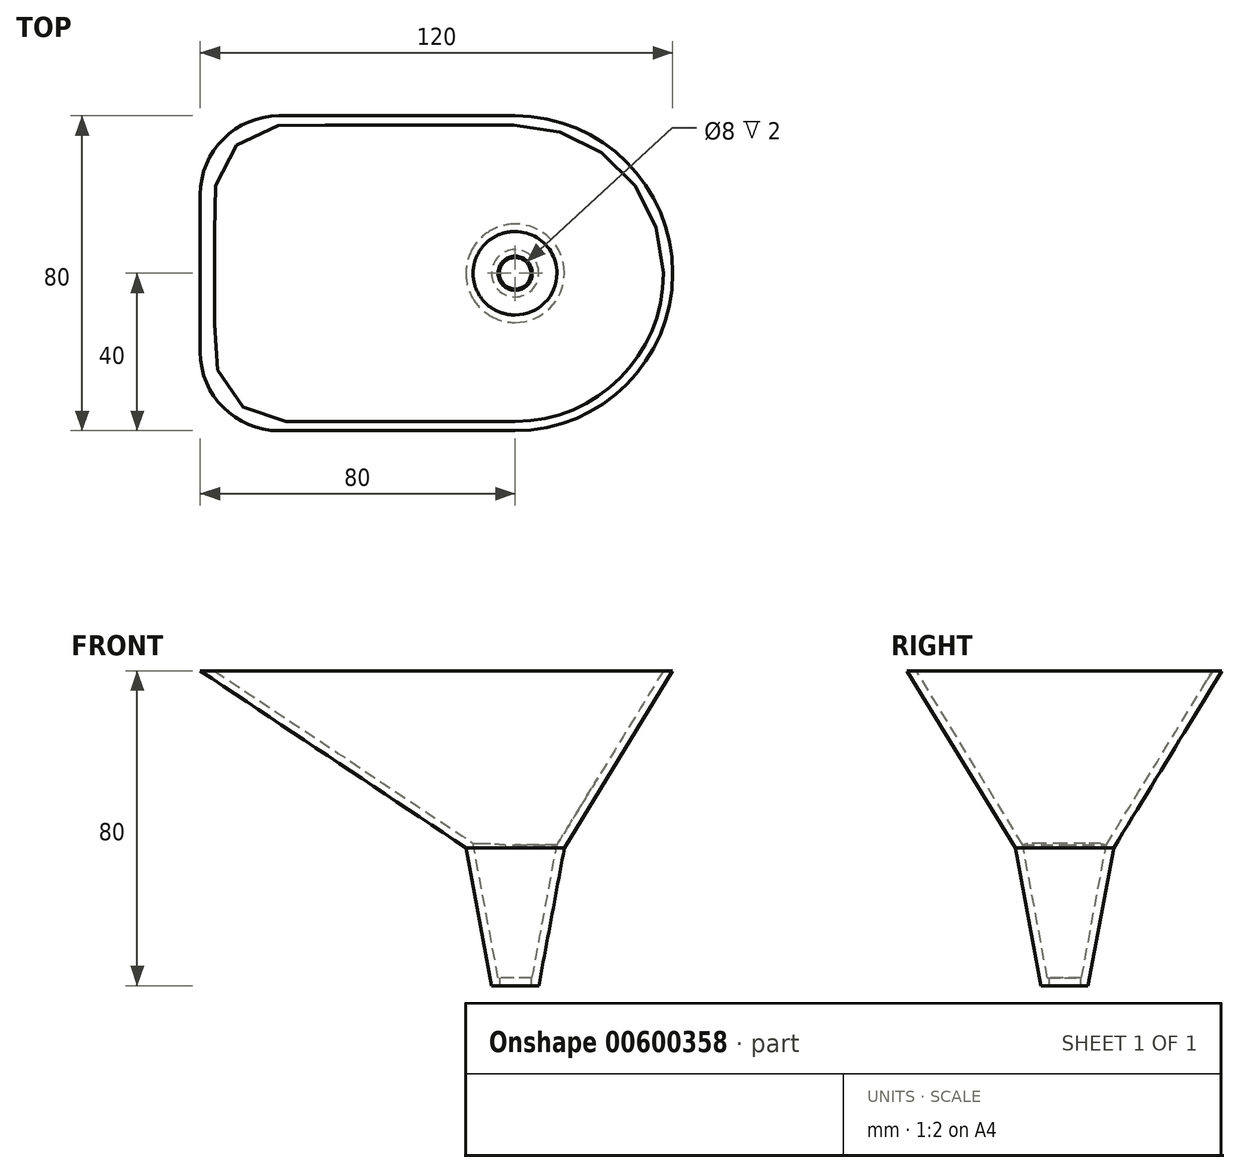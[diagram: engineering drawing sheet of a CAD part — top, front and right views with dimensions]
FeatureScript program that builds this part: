
annotation { "Feature Type Name" : "Feature", "Feature Type Description" : "" }
export const myFeature = defineFeature(function(context is Context, id is Id, definition is map)
    precondition{}
    {
        {
            var Q0;
            Q0=qCreatedBy(makeId("Top.planeOp"),FACE);
            var sketch = newSketch(context, id + "F0", { "sketchPlane" : qUnion([Q0])});
            skCircle(sketch, "E0", {"center": v(0, 0) * mm, "radius": 12.5 * mm});
            skSolve(sketch);
        }
        {
            var Q0;
            Q0=qCreatedBy(makeId("Top.planeOp"),FACE);
            cPlane(context, id + "F1", {"entities" : qUnion([Q0]), "cplaneType" : CPlaneType.OFFSET, "offset" : 35 * mm, "oppositeDirection" : true, "width" : 150 * mm, "height" : 150 * mm});
        }
        {
            var Q0;
            Q0=qCreatedBy(id+"F1.planeOp",FACE);
            var sketch = newSketch(context, id + "F2", { "sketchPlane" : qUnion([Q0])});
            skCircle(sketch, "E1", {"center": v(0, 0) * mm, "radius": 6 * mm});
            skSolve(sketch);
        }
        {
            var Q0;
            Q0=qCreatedBy(makeId("Top.planeOp"),FACE);
            cPlane(context, id + "F3", {"entities" : qUnion([Q0]), "cplaneType" : CPlaneType.OFFSET, "offset" : 45 * mm, "width" : 150 * mm, "height" : 150 * mm});
        }
        {
            var Q0;
            Q0=makeQuery(id+"F2.imprint","IMPRINT",FACE,{"disambiguationData":[TD([[makeQuery(id+"F2.imprint","IMPRINT",EDGE,{"derivedFrom":sQuery(id+"F2.wireOp",EDGE,"E1")}),1.0]])]});
            var Q1;
            Q1=makeQuery(id+"F0.imprint","IMPRINT",FACE,{"disambiguationData":[TD([[makeQuery(id+"F0.imprint","IMPRINT",EDGE,{"derivedFrom":sQuery(id+"F0.wireOp",EDGE,"E0")}),1.0]])]});
            loft(context, id + "F4", {"sheetProfilesArray" : [{ "sheetProfileEntities" : qUnion([Q0]) }, { "sheetProfileEntities" : qUnion([Q1]) }]});
        }
        {
            var Q0;
            Q0=qCreatedBy(id+"F3.planeOp",FACE);
            var sketch = newSketch(context, id + "F5", { "sketchPlane" : qUnion([Q0])});
            skLineSegment(sketch, "E2", {"start": v(0, 40) * mm, "end": v(-60, 40) * mm});
            skLineSegment(sketch, "E3", {"start": v(-80, 20) * mm, "end": v(-80, -20) * mm});
            skLineSegment(sketch, "E4", {"start": v(-60, -40) * mm, "end": v(0, -40) * mm});
            skArc(sketch, "E5", {"start": v(0, 40) * mm, "mid": v(40, 0) * mm, "end": v(0, -40) * mm});
            skPoint(sketch, "E6.visualSharp", {"position": v(-80, 40) * mm});
            skArc(sketch, "E6.filletArc", {"start": v(-60, 40) * mm, "mid": v(-74.14, 34.14) * mm, "end": v(-80, 20) * mm});
            skPoint(sketch, "E7.visualSharp", {"position": v(-80, -40) * mm});
            skArc(sketch, "E7.filletArc", {"start": v(-80, -20) * mm, "mid": v(-74.14, -34.14) * mm, "end": v(-60, -40) * mm});
            skSolve(sketch);
        }
        {
            var Q0;
            Q0=qCreatedBy(makeId("Front.planeOp"),FACE);
            var sketch = newSketch(context, id + "F6", { "sketchPlane" : qUnion([Q0])});
            skLineSegment(sketch, "E8", {"start": v(40, 45) * mm, "end": v(12.5, 0) * mm});
            skLineSegment(sketch, "E9", {"start": v(-80, 45) * mm, "end": v(-12.5, 0) * mm});
            skSolve(sketch);
        }
        {
            var Q0;
            Q0=qCreatedBy(makeId("Right.planeOp"),FACE);
            var sketch = newSketch(context, id + "F7", { "sketchPlane" : qUnion([Q0])});
            skLineSegment(sketch, "E10", {"start": v(-40, 45) * mm, "end": v(-12.5, 0) * mm});
            skLineSegment(sketch, "E11", {"start": v(40, 45) * mm, "end": v(12.5, 0) * mm});
            skSolve(sketch);
        }
        {
            var Q0;
            Q0=makeQuery(id+"F5.imprint","IMPRINT",FACE,{"disambiguationData":[TD([[makeQuery(id+"F5.imprint","IMPRINT",EDGE,{"derivedFrom":sQuery(id+"F5.wireOp",EDGE,"E2")}),1.0]])]});
            var Q1;
            Q1=makeQuery(id+"F0.imprint","IMPRINT",FACE,{"disambiguationData":[TD([[makeQuery(id+"F0.imprint","IMPRINT",EDGE,{"derivedFrom":sQuery(id+"F0.wireOp",EDGE,"E0")}),1.0]])]});
            var Q2;
            Q2=sQuery(id+"F6.wireOp",EDGE,"E8");
            var Q3;
            Q3=sQuery(id+"F6.wireOp",EDGE,"E9");
            var Q4;
            Q4=sQuery(id+"F7.wireOp",EDGE,"E10");
            var Q5;
            Q5=sQuery(id+"F7.wireOp",EDGE,"E11");
            loft(context, id + "F8", {"operationType" : NewBodyOperationType.ADD, "addGuides" : true, "sheetProfilesArray" : [{ "sheetProfileEntities" : qUnion([Q0]) }, { "sheetProfileEntities" : qUnion([Q1]) }], "guidesArray" : [{ "guideEntities" : qUnion([Q2]), "guideDerivativeType" : LoftGuideDerivativeType.DEFAULT, "guideDerivativeMagnitude" : 1 }, { "guideEntities" : qUnion([Q3]), "guideDerivativeType" : LoftGuideDerivativeType.DEFAULT, "guideDerivativeMagnitude" : 1 }, { "guideEntities" : qUnion([Q4]), "guideDerivativeType" : LoftGuideDerivativeType.DEFAULT, "guideDerivativeMagnitude" : 1 }, { "guideEntities" : qUnion([Q5]), "guideDerivativeType" : LoftGuideDerivativeType.DEFAULT, "guideDerivativeMagnitude" : 1 }]});
        }
        {
            var Q0;
            Q0=makeQuery(id+"F8.opLoft","CAP_FACE",FACE,{"disambiguationData":[OSD([makeQuery(id+"F5.imprint","IMPRINT",FACE,{"disambiguationData":[TD([[makeQuery(id+"F5.imprint","IMPRINT",EDGE,{"derivedFrom":sQuery(id+"F5.wireOp",EDGE,"E2")}),1.0]])]})])],"isStart":true});
            shell(context, id + "F9", {"entities" : qUnion([Q0]), "thickness" : 2 * mm});
        }
        {
            var Q0;
            Q0=makeQuery(id+"F2.imprint","IMPRINT",FACE,{"disambiguationData":[TD([[makeQuery(id+"F2.imprint","IMPRINT",EDGE,{"derivedFrom":sQuery(id+"F2.wireOp",EDGE,"E1")}),1.0]])]});
            var sketch = newSketch(context, id + "F10", { "sketchPlane" : qUnion([Q0])});
            skCircle(sketch, "E12", {"center": v(0, 0) * mm, "radius": 4 * mm});
            skSolve(sketch);
        }
        {
            var Q0;
            Q0=makeQuery(id+"F10.imprint","IMPRINT",FACE,{"disambiguationData":[TD([[makeQuery(id+"F10.imprint","IMPRINT",EDGE,{"derivedFrom":sQuery(id+"F10.wireOp",EDGE,"E12")}),1.0]])]});
            var Q1;
            Q1=sQuery(id+"F10.wireOp",EDGE,"E12");
            extrude(context, id + "F11", {"entities" : qUnion([Q0]), "operationType" : NewBodyOperationType.REMOVE, "surfaceEntities" : qUnion([Q1]), "endBound" : BoundingType.THROUGH_ALL, "depth" : 25 * mm, "offsetDistance" : 25 * mm});
        }
    });
